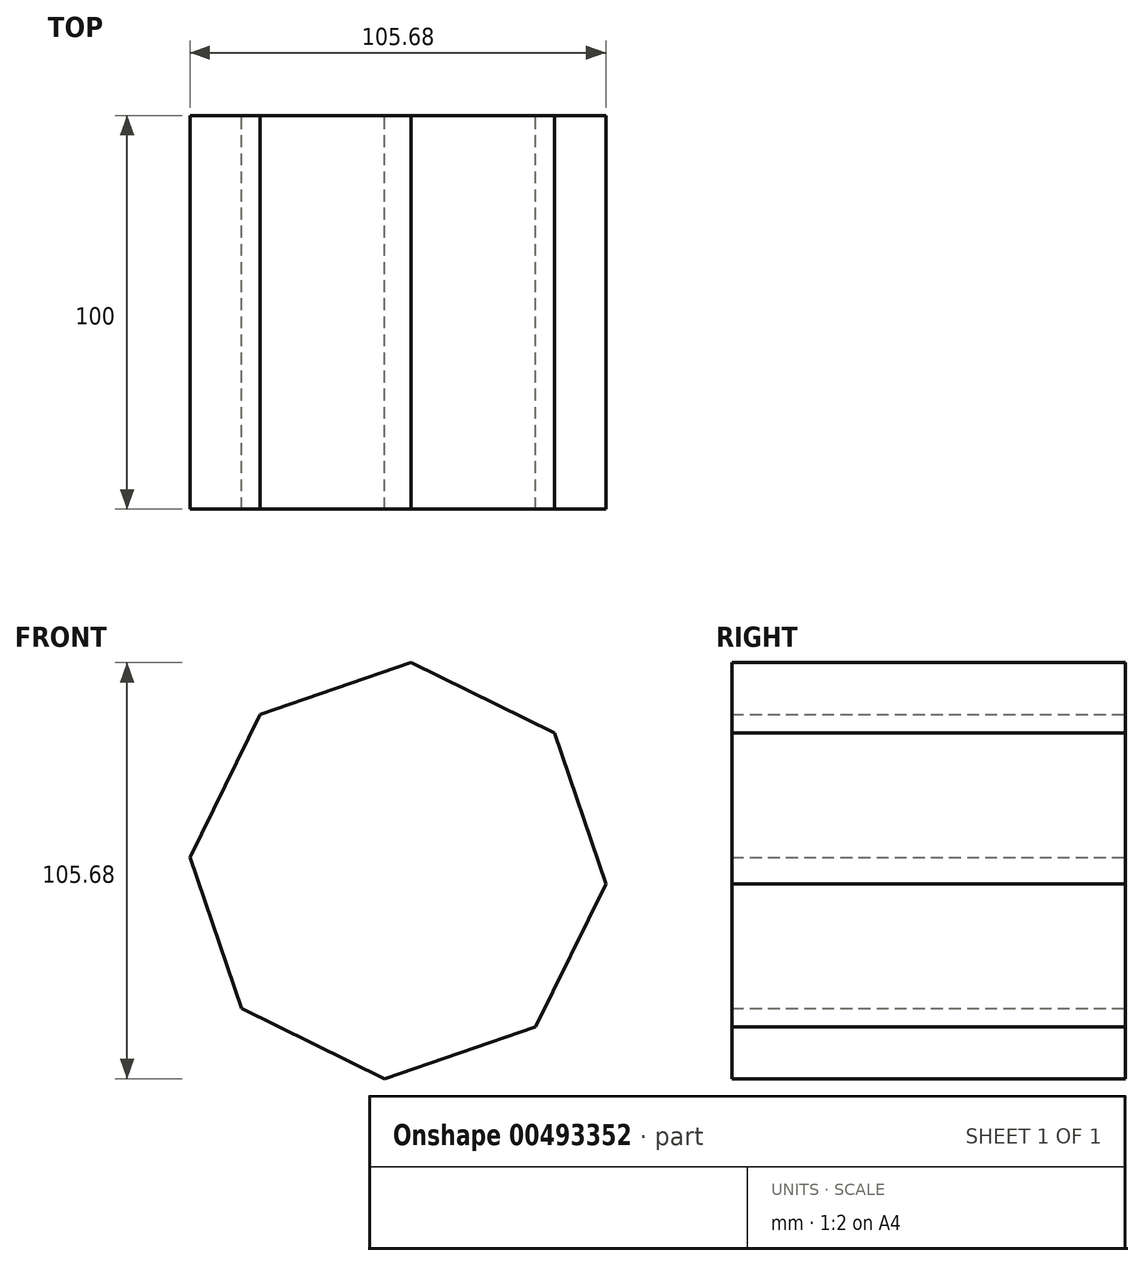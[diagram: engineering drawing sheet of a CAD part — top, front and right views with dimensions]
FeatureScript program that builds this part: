
annotation { "Feature Type Name" : "Feature", "Feature Type Description" : "" }
export const myFeature = defineFeature(function(context is Context, id is Id, definition is map)
    precondition{}
    {
        {
            var Q0;
            Q0=qCreatedBy(makeId("Front.planeOp"),FACE);
            var sketch = newSketch(context, id + "F0", { "sketchPlane" : qUnion([Q0])});
            skCircle(sketch, "E0.cCircle", {"center": v(0, 0) * mm, "radius": 52.95 * mm, "construction": true});
            skLineSegment(sketch, "E0.0", {"start": v(-35, 39.73) * mm, "end": v(3.35, 52.84) * mm});
            skLineSegment(sketch, "E0.1", {"start": v(3.35, 52.84) * mm, "end": v(39.73, 35) * mm});
            skLineSegment(sketch, "E0.2", {"start": v(39.73, 35) * mm, "end": v(52.84, -3.35) * mm});
            skLineSegment(sketch, "E0.3", {"start": v(52.84, -3.35) * mm, "end": v(35, -39.73) * mm});
            skLineSegment(sketch, "E0.4", {"start": v(35, -39.73) * mm, "end": v(-3.35, -52.84) * mm});
            skLineSegment(sketch, "E0.5", {"start": v(-3.35, -52.84) * mm, "end": v(-39.73, -35) * mm});
            skLineSegment(sketch, "E0.6", {"start": v(-39.73, -35) * mm, "end": v(-52.84, 3.35) * mm});
            skLineSegment(sketch, "E0.7", {"start": v(-52.84, 3.35) * mm, "end": v(-35, 39.73) * mm});
            skSolve(sketch);
        }
        {
            var Q0;
            Q0 = qSketchRegion(id + "F0", true);
            extrude(context, id + "F1", {"entities" : qUnion([Q0]), "endBound" : BoundingType.SYMMETRIC, "depth" : 100 * mm});
        }
    });
